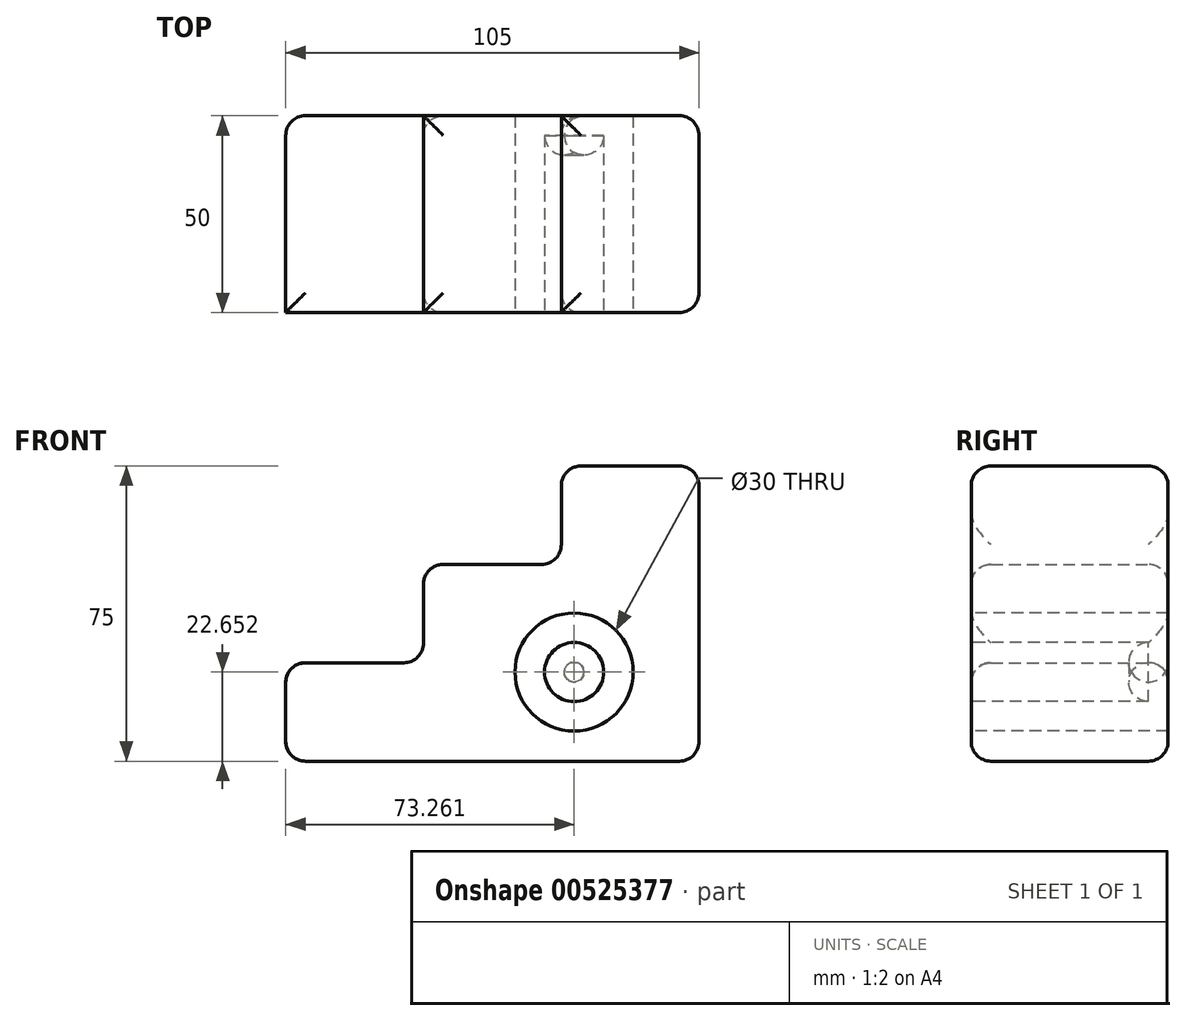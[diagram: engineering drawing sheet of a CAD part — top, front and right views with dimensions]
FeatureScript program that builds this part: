
annotation { "Feature Type Name" : "Feature", "Feature Type Description" : "" }
export const myFeature = defineFeature(function(context is Context, id is Id, definition is map)
    precondition{}
    {
        {
            var Q0;
            Q0=qCreatedBy(makeId("Front.planeOp"),FACE);
            var sketch = newSketch(context, id + "F0", { "sketchPlane" : qUnion([Q0])});
            skLineSegment(sketch, "E0", {"start": v(-66.2, -0.07) * mm, "end": v(38.8, -0.07) * mm});
            skLineSegment(sketch, "E1", {"start": v(38.8, -0.07) * mm, "end": v(38.8, 74.93) * mm});
            skLineSegment(sketch, "E2", {"start": v(38.8, 74.93) * mm, "end": v(3.8, 74.93) * mm});
            skLineSegment(sketch, "E3", {"start": v(3.8, 74.93) * mm, "end": v(3.8, 49.93) * mm});
            skLineSegment(sketch, "E4", {"start": v(3.8, 49.93) * mm, "end": v(-31.2, 49.93) * mm});
            skLineSegment(sketch, "E5", {"start": v(-31.2, 49.93) * mm, "end": v(-31.2, 24.93) * mm});
            skLineSegment(sketch, "E6", {"start": v(-31.2, 24.93) * mm, "end": v(-66.2, 24.93) * mm});
            skLineSegment(sketch, "E7", {"start": v(-66.2, 24.93) * mm, "end": v(-66.2, -0.07) * mm});
            skSolve(sketch);
        }
        {
            var Q0;
            Q0 = qSketchRegion(id + "F0", true);
            extrude(context, id + "F1", {"entities" : qUnion([Q0]), "depth" : 50 * mm, "offsetDistance" : 25 * mm});
        }
        {
            var Q0;
            Q0=makeQuery(id+"F1.opExtrude","CAP_FACE",FACE,{"disambiguationData":[OSD([sQuery(id+"F0.wireOp",EDGE,"E0"),sQuery(id+"F0.wireOp",EDGE,"E1"),sQuery(id+"F0.wireOp",EDGE,"E2"),sQuery(id+"F0.wireOp",EDGE,"E3"),sQuery(id+"F0.wireOp",EDGE,"E4"),sQuery(id+"F0.wireOp",EDGE,"E5"),sQuery(id+"F0.wireOp",EDGE,"E6"),sQuery(id+"F0.wireOp",EDGE,"E7")])],"isStart":false});
            var sketch = newSketch(context, id + "F2", { "sketchPlane" : qUnion([Q0])});
            skCircle(sketch, "E8", {"center": v(7.07, 22.58) * mm, "radius": 15 * mm});
            skCircle(sketch, "E9", {"center": v(7.07, 22.58) * mm, "radius": 7.5 * mm});
            skSolve(sketch);
        }
        {
            var Q0;
            Q0=makeQuery(id+"F2.imprint","IMPRINT",FACE,{"disambiguationData":[TD([[makeQuery(id+"F2.imprint","IMPRINT",EDGE,{"derivedFrom":sQuery(id+"F2.wireOp",EDGE,"E8")}),1.0]])]});
            extrude(context, id + "F3", {"entities" : qUnion([Q0]), "operationType" : NewBodyOperationType.REMOVE, "endBound" : BoundingType.UP_TO_NEXT, "oppositeDirection" : true, "depth" : 30 * mm, "offsetDistance" : 25 * mm});
        }
        {
            var Q0;
            Q0=makeQuery(id+"F1.opExtrude","SWEPT_EDGE",EDGE,{"disambiguationData":[OSD([sQuery(id+"F0.wireOp",EDGE,"E6"),sQuery(id+"F0.wireOp",EDGE,"E7")])]});
            var Q1;
            Q1=makeQuery(id+"F1.opExtrude","SWEPT_EDGE",EDGE,{"disambiguationData":[OSD([sQuery(id+"F0.wireOp",EDGE,"E5"),sQuery(id+"F0.wireOp",EDGE,"E6")])]});
            var Q2;
            Q2=makeQuery(id+"F1.opExtrude","SWEPT_EDGE",EDGE,{"disambiguationData":[OSD([sQuery(id+"F0.wireOp",EDGE,"E4"),sQuery(id+"F0.wireOp",EDGE,"E5")])]});
            var Q3;
            Q3=makeQuery(id+"F1.opExtrude","SWEPT_EDGE",EDGE,{"disambiguationData":[OSD([sQuery(id+"F0.wireOp",EDGE,"E3"),sQuery(id+"F0.wireOp",EDGE,"E4")])]});
            var Q4;
            Q4=makeQuery(id+"F1.opExtrude","SWEPT_EDGE",EDGE,{"disambiguationData":[OSD([sQuery(id+"F0.wireOp",EDGE,"E2"),sQuery(id+"F0.wireOp",EDGE,"E3")])]});
            var Q5;
            Q5=makeQuery(id+"F1.opExtrude","SWEPT_FACE",FACE,{"disambiguationData":[OSD([sQuery(id+"F0.wireOp",EDGE,"E2")])]});
            var Q6;
            Q6=makeQuery(id+"F1.opExtrude","CAP_EDGE",EDGE,{"disambiguationData":[OSD([sQuery(id+"F0.wireOp",EDGE,"E4")])],"isStart":false});
            var Q7;
            Q7=makeQuery(id+"F1.opExtrude","CAP_EDGE",EDGE,{"disambiguationData":[OSD([sQuery(id+"F0.wireOp",EDGE,"E6")])],"isStart":false});
            var Q8;
            Q8=makeQuery(id+"F1.opExtrude","CAP_EDGE",EDGE,{"disambiguationData":[OSD([sQuery(id+"F0.wireOp",EDGE,"E4")])],"isStart":true});
            var Q9;
            Q9=makeQuery(id+"F1.opExtrude","CAP_EDGE",EDGE,{"disambiguationData":[OSD([sQuery(id+"F0.wireOp",EDGE,"E6")])],"isStart":true});
            var Q10;
            Q10=makeQuery(id+"F3.boolean.opBoolean","COPY",EDGE,{"derivedFrom":makeQuery(id+"F3.opExtrude","CAP_EDGE",EDGE,{"disambiguationData":[OSD([sQuery(id+"F2.wireOp",EDGE,"E8")])],"isStart":false})});
            var Q11;
            Q11=makeQuery(id+"F3.boolean.opBoolean","COPY",EDGE,{"derivedFrom":makeQuery(id+"F3.opExtrude","CAP_EDGE",EDGE,{"disambiguationData":[OSD([sQuery(id+"F2.wireOp",EDGE,"E9")])],"isStart":false})});
            var Q12;
            Q12=makeQuery(id+"F1.opExtrude","CAP_EDGE",EDGE,{"disambiguationData":[OSD([sQuery(id+"F0.wireOp",EDGE,"E0")])],"isStart":false});
            var Q13;
            Q13=makeQuery(id+"F1.opExtrude","SWEPT_EDGE",EDGE,{"disambiguationData":[OSD([sQuery(id+"F0.wireOp",EDGE,"E0"),sQuery(id+"F0.wireOp",EDGE,"E7")])]});
            var Q14;
            Q14=makeQuery(id+"F1.opExtrude","SWEPT_EDGE",EDGE,{"disambiguationData":[OSD([sQuery(id+"F0.wireOp",EDGE,"E0"),sQuery(id+"F0.wireOp",EDGE,"E1")])]});
            var Q15;
            Q15=makeQuery(id+"F1.opExtrude","CAP_EDGE",EDGE,{"disambiguationData":[OSD([sQuery(id+"F0.wireOp",EDGE,"E0")])],"isStart":true});
            var Q16;
            Q16=makeQuery(id+"F1.opExtrude","CAP_EDGE",EDGE,{"disambiguationData":[OSD([sQuery(id+"F0.wireOp",EDGE,"E1")])],"isStart":true});
            var Q17;
            Q17=makeQuery(id+"F1.opExtrude","CAP_EDGE",EDGE,{"disambiguationData":[OSD([sQuery(id+"F0.wireOp",EDGE,"E7")])],"isStart":true});
            var Q18;
            Q18=makeQuery(id+"F1.opExtrude","CAP_EDGE",EDGE,{"disambiguationData":[OSD([sQuery(id+"F0.wireOp",EDGE,"E1")])],"isStart":false});
            fillet(context, id + "F4", {"entities" : qUnion([Q0, Q1, Q2, Q3, Q4, Q5, Q6, Q7, Q8, Q9, Q10, Q11, Q12, Q13, Q14, Q15, Q16, Q17, Q18]), "radius" : 5 * mm, "tangentPropagation" : true, "allowEdgeOverflow" : false});
        }
    });
